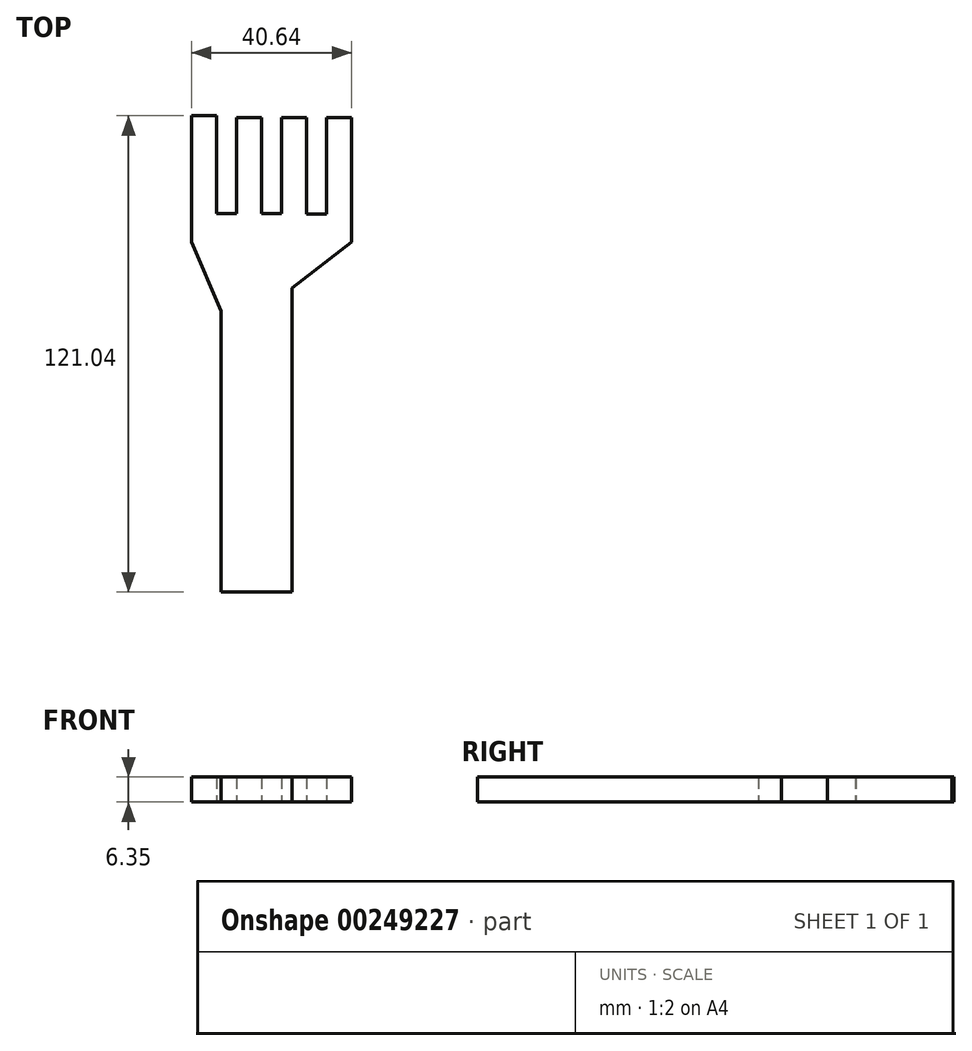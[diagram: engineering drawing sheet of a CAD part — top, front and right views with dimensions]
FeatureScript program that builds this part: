
annotation { "Feature Type Name" : "Feature", "Feature Type Description" : "" }
export const myFeature = defineFeature(function(context is Context, id is Id, definition is map)
    precondition{}
    {
        {
            var Q0;
            Q0=qCreatedBy(makeId("Top.planeOp"),FACE);
            var sketch = newSketch(context, id + "F0", { "sketchPlane" : qUnion([Q0])});
            skLineSegment(sketch, "E0", {"start": v(-3.98, -42.73) * mm, "end": v(14.15, -42.73) * mm});
            skLineSegment(sketch, "E1", {"start": v(14.15, -42.73) * mm, "end": v(14.15, 34.51) * mm});
            skLineSegment(sketch, "E2", {"start": v(14.15, 34.51) * mm, "end": v(29.21, 46.17) * mm});
            skLineSegment(sketch, "E3", {"start": v(29.21, 46.17) * mm, "end": v(29.21, 77.8) * mm});
            skLineSegment(sketch, "E4", {"start": v(29.21, 77.8) * mm, "end": v(22.86, 77.8) * mm});
            skLineSegment(sketch, "E5", {"start": v(22.86, 77.8) * mm, "end": v(22.86, 53.31) * mm});
            skLineSegment(sketch, "E6", {"start": v(22.86, 53.31) * mm, "end": v(17.78, 53.31) * mm});
            skLineSegment(sketch, "E7", {"start": v(17.78, 53.31) * mm, "end": v(17.78, 77.8) * mm});
            skLineSegment(sketch, "E8", {"start": v(17.78, 77.8) * mm, "end": v(11.43, 77.8) * mm});
            skLineSegment(sketch, "E9", {"start": v(11.43, 77.8) * mm, "end": v(11.43, 53.45) * mm});
            skLineSegment(sketch, "E10", {"start": v(11.43, 53.45) * mm, "end": v(6.35, 53.45) * mm});
            skLineSegment(sketch, "E11", {"start": v(6.35, 53.45) * mm, "end": v(6.35, 77.8) * mm});
            skLineSegment(sketch, "E12", {"start": v(6.35, 77.8) * mm, "end": v(0, 77.8) * mm});
            skLineSegment(sketch, "E13", {"start": v(0, 77.8) * mm, "end": v(0, 53.45) * mm});
            skLineSegment(sketch, "E14", {"start": v(0, 53.45) * mm, "end": v(-5.08, 53.45) * mm});
            skLineSegment(sketch, "E15", {"start": v(-5.08, 53.45) * mm, "end": v(-5.08, 78.3) * mm});
            skLineSegment(sketch, "E16", {"start": v(-5.08, 78.3) * mm, "end": v(-11.43, 78.3) * mm});
            skLineSegment(sketch, "E17", {"start": v(-11.43, 78.3) * mm, "end": v(-11.43, 46.17) * mm});
            skLineSegment(sketch, "E18", {"start": v(-3.98, -42.73) * mm, "end": v(-3.98, 28.64) * mm});
            skLineSegment(sketch, "E19", {"start": v(-3.98, 28.64) * mm, "end": v(-11.43, 46.17) * mm});
            skSolve(sketch);
        }
        {
            var Q0;
            Q0=makeQuery(id+"F0.imprint","IMPRINT",FACE,{"disambiguationData":[TD([[makeQuery(id+"F0.imprint","IMPRINT",EDGE,{"derivedFrom":sQuery(id+"F0.wireOp",EDGE,"E0")}),1.0]])]});
            extrude(context, id + "F1", {"entities" : qUnion([Q0]), "depth" : 6.35 * mm});
        }
    });
